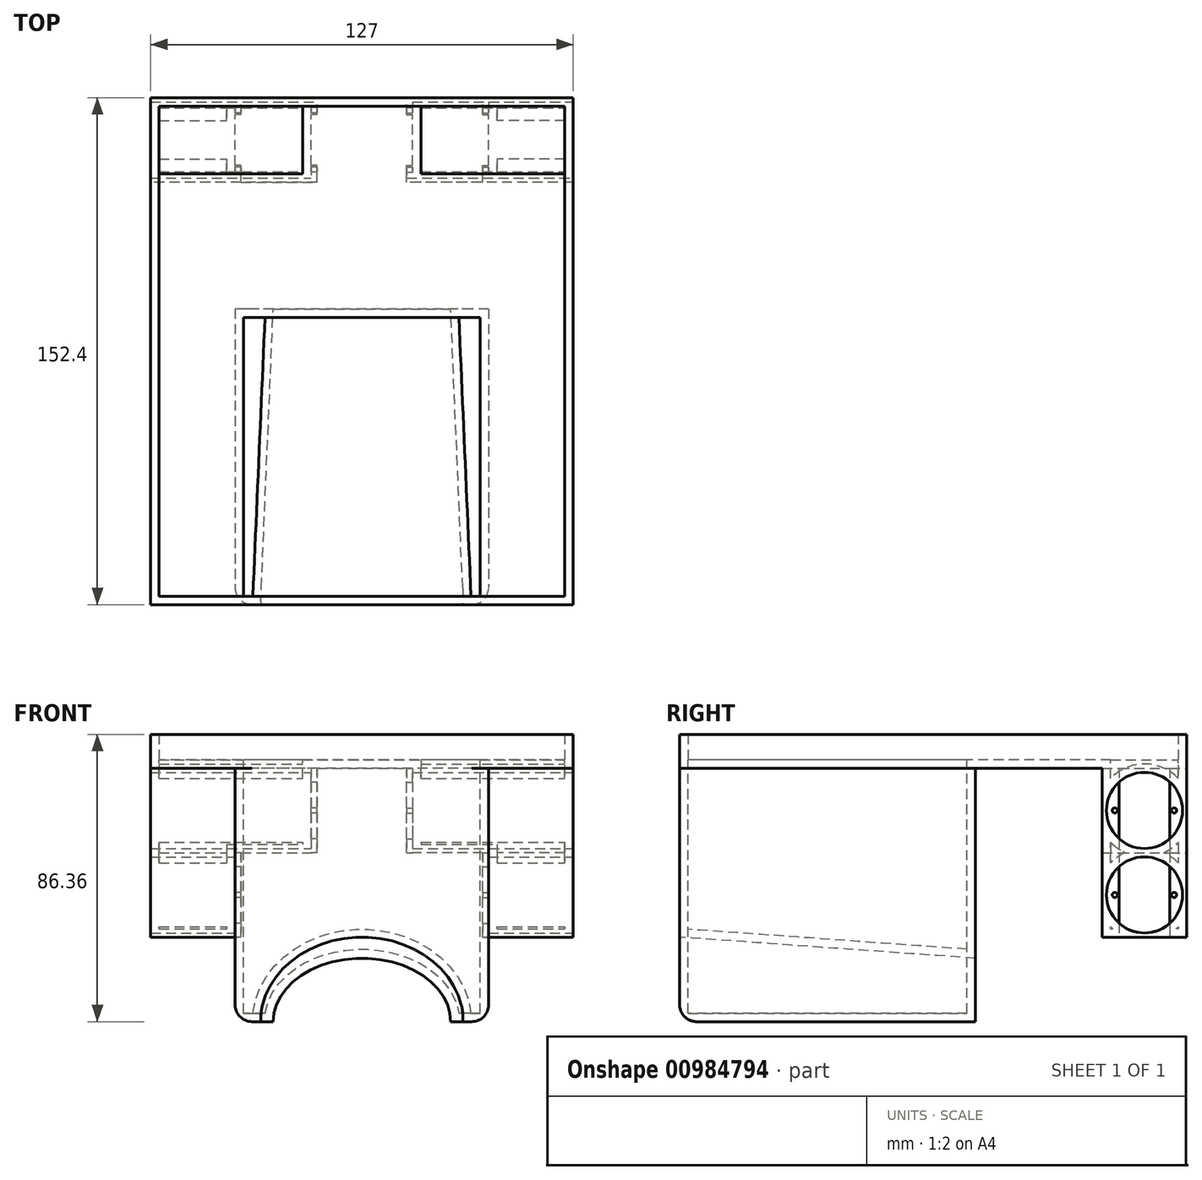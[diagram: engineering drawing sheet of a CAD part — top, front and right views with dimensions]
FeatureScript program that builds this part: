
annotation { "Feature Type Name" : "Feature", "Feature Type Description" : "" }
export const myFeature = defineFeature(function(context is Context, id is Id, definition is map)
    precondition{}
    {
        {
            var Q0;
            Q0=qCreatedBy(makeId("Top.planeOp"),FACE);
            var sketch = newSketch(context, id + "F0", { "sketchPlane" : qUnion([Q0])});
            skLineSegment(sketch, "E0.bottom", {"start": v(-89.57, 110.43) * mm, "end": v(12.03, 110.43) * mm});
            skLineSegment(sketch, "E0.top", {"start": v(-89.57, -41.97) * mm, "end": v(12.03, -41.97) * mm});
            skLineSegment(sketch, "E0.left", {"start": v(-89.57, 110.43) * mm, "end": v(-89.57, -41.97) * mm});
            skLineSegment(sketch, "E0.right", {"start": v(12.03, 110.43) * mm, "end": v(12.03, -41.97) * mm});
            skLineSegment(sketch, "E1", {"start": v(12.03, 110.43) * mm, "end": v(24.73, 110.43) * mm});
            skLineSegment(sketch, "E2", {"start": v(24.73, 110.43) * mm, "end": v(24.73, -41.97) * mm});
            skLineSegment(sketch, "E3", {"start": v(24.73, -41.97) * mm, "end": v(12.03, -41.97) * mm});
            skLineSegment(sketch, "E4.bottom", {"start": v(-89.57, 110.43) * mm, "end": v(-102.27, 110.43) * mm});
            skLineSegment(sketch, "E4.top", {"start": v(-89.57, -41.97) * mm, "end": v(-102.27, -41.97) * mm});
            skLineSegment(sketch, "E4.right", {"start": v(-102.27, 110.43) * mm, "end": v(-102.27, -41.97) * mm});
            skSolve(sketch);
        }
        {
            var Q0;
            Q0=makeQuery(id+"F0.imprint","IMPRINT",FACE,{"disambiguationData":[TD([[makeQuery(id+"F0.imprint","IMPRINT",EDGE,{"derivedFrom":sQuery(id+"F0.wireOp",EDGE,"E0.bottom")}),-1.0]])]});
            var Q1;
            Q1=makeQuery(id+"F0.imprint","IMPRINT",FACE,{"disambiguationData":[TD([[makeQuery(id+"F0.imprint","IMPRINT",EDGE,{"derivedFrom":sQuery(id+"F0.wireOp",EDGE,"E0.right")}),1.0]])]});
            var Q2;
            Q2=makeQuery(id+"F0.imprint","IMPRINT",FACE,{"disambiguationData":[TD([[makeQuery(id+"F0.imprint","IMPRINT",EDGE,{"derivedFrom":sQuery(id+"F0.wireOp",EDGE,"E4.bottom")}),1.0]])]});
            extrude(context, id + "F1", {"entities" : qUnion([Q0, Q1, Q2]), "depth" : 10.16 * mm, "offsetDistance" : 25.4 * mm});
        }
        {
            var Q0;
            Q0=makeQuery(id+"F1.opExtrude","CAP_FACE",FACE,{"disambiguationData":[OSD([sQuery(id+"F0.wireOp",EDGE,"E0.bottom"),sQuery(id+"F0.wireOp",EDGE,"E0.top"),sQuery(id+"F0.wireOp",EDGE,"E0.left"),sQuery(id+"F0.wireOp",EDGE,"E0.right")])],"isStart":true});
            var sketch = newSketch(context, id + "F2", { "sketchPlane" : qUnion([Q0])});
            skLineSegment(sketch, "E5", {"start": v(-38.77, -110.43) * mm, "end": v(-38.77, 53.26) * mm, "construction": true});
            skPoint(sketch, "E5.endSnap0", {"position": v(-38.77, 41.97) * mm});
            skLineSegment(sketch, "E6.bottom", {"start": v(-0.67, -46.93) * mm, "end": v(-76.87, -46.93) * mm});
            skLineSegment(sketch, "E6.top", {"start": v(-0.67, 41.97) * mm, "end": v(-76.87, 41.97) * mm});
            skLineSegment(sketch, "E6.left", {"start": v(-0.67, -46.93) * mm, "end": v(-0.67, 41.97) * mm});
            skLineSegment(sketch, "E6.right", {"start": v(-76.87, -46.93) * mm, "end": v(-76.87, 41.97) * mm});
            skLineSegment(sketch, "E7", {"start": v(-102.27, -34.23) * mm, "end": v(125.7, -34.23) * mm, "construction": true});
            skSolve(sketch);
        }
        {
            var Q0;
            Q0=makeQuery(id+"F2.imprint","IMPRINT",FACE,{"disambiguationData":[TD([[makeQuery(id+"F2.imprint","IMPRINT",EDGE,{"derivedFrom":sQuery(id+"F2.wireOp",EDGE,"E6.bottom")}),-1.0]])]});
            extrude(context, id + "F3", {"entities" : qUnion([Q0]), "operationType" : NewBodyOperationType.ADD, "depth" : 76.2 * mm, "offsetDistance" : 25.4 * mm});
        }
        {
            var Q0;
            Q0=makeQuery(id+"F3.boolean.opBoolean","MERGE",FACE,{"derivedFrom":[makeQuery(id+"F1.opExtrude","SWEPT_FACE",FACE,{"disambiguationData":[OSD([sQuery(id+"F0.wireOp",EDGE,"E0.top")])]}),makeQuery(id+"F3.opExtrude","SWEPT_FACE",FACE,{"disambiguationData":[OSD([sQuery(id+"F2.wireOp",EDGE,"E6.top")])]})]});
            var sketch = newSketch(context, id + "F4", { "sketchPlane" : qUnion([Q0])});
            skEllipse(sketch, "E8", {"center": v(-38.77, -76.2) * mm, "majorRadius": 30.48 * mm, "minorRadius": 25.4 * mm, "majorAxis": v(-1, 0)});
            skSolve(sketch);
        }
        {
            var Q0;
            Q0=makeQuery(id+"F3.opExtrude","SWEPT_FACE",FACE,{"disambiguationData":[OSD([sQuery(id+"F2.wireOp",EDGE,"E6.bottom")])]});
            var sketch = newSketch(context, id + "F5", { "sketchPlane" : qUnion([Q0])});
            skEllipse(sketch, "E9", {"center": v(38.77, -76.2) * mm, "majorRadius": 26.67 * mm, "minorRadius": 19.05 * mm, "majorAxis": v(-1, 0)});
            skSolve(sketch);
        }
        {
            var Q1;
            {var subQ0=sQuery(id+"F4.wireOp",EDGE,"E8");var subQ1=makeQuery(id+"F3.opExtrude","CAP_EDGE",EDGE,{"disambiguationData":[OSD([sQuery(id+"F2.wireOp",EDGE,"E6.top")])],"isStart":false});var subQ2=makeQuery(id+"F4.imprint","INTERSECT",VERTEX,{"disambiguationData":[OD(0.0)],"derivedFrom":[subQ1,subQ0]});Q1=makeQuery(id+"F4.imprint","IMPRINT",FACE,{"disambiguationData":[TD([[makeQuery(id+"F4.imprint","IMPRINT",EDGE,{"disambiguationData":[TD([[subQ2,1.0]])],"derivedFrom":subQ0}),1.0]])]});}
            var Q2;
            {var subQ0=sQuery(id+"F5.wireOp",EDGE,"E9");var subQ1=makeQuery(id+"F3.opExtrude","CAP_EDGE",EDGE,{"disambiguationData":[OSD([sQuery(id+"F2.wireOp",EDGE,"E6.bottom")])],"isStart":false});var subQ2=makeQuery(id+"F5.imprint","INTERSECT",VERTEX,{"disambiguationData":[OD(0.0)],"derivedFrom":[subQ1,subQ0]});Q2=makeQuery(id+"F5.imprint","IMPRINT",FACE,{"disambiguationData":[TD([[makeQuery(id+"F5.imprint","IMPRINT",EDGE,{"disambiguationData":[TD([[subQ2,1.0]])],"derivedFrom":subQ0}),1.0]])]});}
            loft(context, id + "F6", {"operationType" : NewBodyOperationType.REMOVE, "sheetProfilesArray" : [{ "sheetProfileEntities" : qUnion([Q1]) }, { "sheetProfileEntities" : qUnion([Q2]) }]});
        }
        {
            var Q0;
            Q0=makeQuery(id+"F0.imprint","IMPRINT",FACE,{"disambiguationData":[TD([[makeQuery(id+"F0.imprint","IMPRINT",EDGE,{"derivedFrom":sQuery(id+"F0.wireOp",EDGE,"E0.right")}),1.0]])]});
            extrude(context, id + "F7", {"entities" : qUnion([Q0]), "operationType" : NewBodyOperationType.ADD, "depth" : 10.16 * mm, "offsetDistance" : 25.4 * mm});
        }
        {
            var Q0;
            Q0=makeQuery(id+"F1.opExtrude","CAP_FACE",FACE,{"disambiguationData":[OSD([sQuery(id+"F0.wireOp",EDGE,"E0.bottom"),sQuery(id+"F0.wireOp",EDGE,"E0.top"),sQuery(id+"F0.wireOp",EDGE,"E1"),sQuery(id+"F0.wireOp",EDGE,"E2"),sQuery(id+"F0.wireOp",EDGE,"E3"),sQuery(id+"F0.wireOp",EDGE,"E4.bottom"),sQuery(id+"F0.wireOp",EDGE,"E4.top"),sQuery(id+"F0.wireOp",EDGE,"E4.right")])],"isStart":true});
            var sketch = newSketch(context, id + "F8", { "sketchPlane" : qUnion([Q0])});
            skLineSegment(sketch, "E10.bottom", {"start": v(24.73, -110.43) * mm, "end": v(-102.27, -110.43) * mm});
            skLineSegment(sketch, "E10.top", {"start": v(24.73, -85.03) * mm, "end": v(-102.27, -85.03) * mm});
            skLineSegment(sketch, "E10.left", {"start": v(24.73, -110.43) * mm, "end": v(24.73, -85.03) * mm});
            skLineSegment(sketch, "E10.right", {"start": v(-102.27, -110.43) * mm, "end": v(-102.27, -85.03) * mm});
            skSolve(sketch);
        }
        {
            var Q0;
            Q0=makeQuery(id+"F8.imprint","IMPRINT",FACE,{"disambiguationData":[TD([[makeQuery(id+"F8.imprint","IMPRINT",EDGE,{"derivedFrom":sQuery(id+"F8.wireOp",EDGE,"E10.bottom")}),1.0]])]});
            extrude(context, id + "F9", {"entities" : qUnion([Q0]), "operationType" : NewBodyOperationType.ADD, "depth" : 50.8 * mm, "offsetDistance" : 25.4 * mm});
        }
        {
            var Q0;
            Q0=makeQuery(id+"F9.boolean.opBoolean","MERGE",FACE,{"derivedFrom":[makeQuery(id+"F1.opExtrude","SWEPT_FACE",FACE,{"disambiguationData":[OSD([sQuery(id+"F0.wireOp",EDGE,"E0.bottom"),sQuery(id+"F0.wireOp",EDGE,"E1"),sQuery(id+"F0.wireOp",EDGE,"E4.bottom")])]}),makeQuery(id+"F9.opExtrude","SWEPT_FACE",FACE,{"disambiguationData":[OSD([sQuery(id+"F8.wireOp",EDGE,"E10.bottom")])]})]});
            var sketch = newSketch(context, id + "F10", { "sketchPlane" : qUnion([Q0])});
            skLineSegment(sketch, "E11", {"start": v(0.67, -50.8) * mm, "end": v(0.67, -25.4) * mm});
            skLineSegment(sketch, "E12", {"start": v(0.67, -25.4) * mm, "end": v(23.53, -25.4) * mm});
            skLineSegment(sketch, "E13", {"start": v(23.53, -25.4) * mm, "end": v(23.53, 0) * mm});
            skLineSegment(sketch, "E14", {"start": v(23.53, 0) * mm, "end": v(38.77, 0) * mm});
            skLineSegment(sketch, "E15", {"start": v(38.77, -50.8) * mm, "end": v(38.77, 29.87) * mm, "construction": true});
            skPoint(sketch, "E15.endSnap0", {"position": v(38.77, 10.16) * mm});
            skLineSegment(sketch, "E16.MirrorCS", {"start": v(54, -25.4) * mm, "end": v(54, 0) * mm});
            skLineSegment(sketch, "E17.MirrorCS", {"start": v(54, 0) * mm, "end": v(38.77, 0) * mm});
            skLineSegment(sketch, "E18.MirrorCS", {"start": v(76.87, -25.4) * mm, "end": v(54, -25.4) * mm});
            skLineSegment(sketch, "E19.MirrorCS", {"start": v(76.87, -50.8) * mm, "end": v(76.87, -25.4) * mm});
            skSolve(sketch);
        }
        {
            var Q0;
            {var subQ1=sQuery(id+"F10.wireOp",EDGE,"E11");Q0=makeQuery(id+"F10.imprint","IMPRINT",FACE,{"disambiguationData":[TD([[makeQuery(id+"F10.imprint","IMPRINT",EDGE,{"derivedFrom":subQ1}),-1.0]])]});}
            extrude(context, id + "F11", {"entities" : qUnion([Q0]), "operationType" : NewBodyOperationType.REMOVE, "oppositeDirection" : true, "depth" : 25.4 * mm, "offsetDistance" : 25.4 * mm});
        }
        {
            var Q0;
            Q0=makeQuery(id+"F9.boolean.opBoolean","MERGE",FACE,{"derivedFrom":[makeQuery(id+"F1.opExtrude","SWEPT_FACE",FACE,{"disambiguationData":[OSD([sQuery(id+"F0.wireOp",EDGE,"E2")])]}),makeQuery(id+"F9.opExtrude","SWEPT_FACE",FACE,{"disambiguationData":[OSD([sQuery(id+"F8.wireOp",EDGE,"E10.left")])]})]});
            var sketch = newSketch(context, id + "F12", { "sketchPlane" : qUnion([Q0])});
            skLineSegment(sketch, "E20", {"start": v(97.73, -50.8) * mm, "end": v(97.73, 17.2) * mm, "construction": true});
            skLineSegment(sketch, "E21", {"start": v(110.43, -38.1) * mm, "end": v(64.46, -38.1) * mm, "construction": true});
            skCircle(sketch, "E22", {"center": v(97.73, -38.1) * mm, "radius": 11.43 * mm});
            skCircle(sketch, "E23.0.1.0", {"center": v(97.73, -12.7) * mm, "radius": 11.43 * mm});
            skLineSegment(sketch, "E23.direction1", {"start": v(97.73, -38.1) * mm, "end": v(123.13, -38.1) * mm, "construction": true});
            skLineSegment(sketch, "E23.direction2", {"start": v(97.73, -38.1) * mm, "end": v(97.73, -12.7) * mm, "construction": true});
            skSolve(sketch);
        }
        {
            var Q0;
            Q0=makeQuery(id+"F12.imprint","IMPRINT",FACE,{"disambiguationData":[TD([[makeQuery(id+"F12.imprint","IMPRINT",EDGE,{"derivedFrom":sQuery(id+"F12.wireOp",EDGE,"E22")}),1.0]])]});
            var Q1;
            Q1=makeQuery(id+"F12.imprint","IMPRINT",FACE,{"disambiguationData":[TD([[makeQuery(id+"F12.imprint","IMPRINT",EDGE,{"derivedFrom":sQuery(id+"F12.wireOp",EDGE,"E23.0.1.0")}),1.0]])]});
            extrude(context, id + "F13", {"entities" : qUnion([Q0, Q1]), "operationType" : NewBodyOperationType.REMOVE, "endBound" : BoundingType.THROUGH_ALL, "oppositeDirection" : true, "depth" : 25.4 * mm, "offsetDistance" : 25.4 * mm});
        }
        {
            var Q0;
            Q0=makeQuery(id+"F11.boolean.opBoolean","COPY",FACE,{"derivedFrom":makeQuery(id+"F11.opExtrude","SWEPT_FACE",FACE,{"disambiguationData":[OSD([sQuery(id+"F10.wireOp",EDGE,"E11")])]})});
            var sketch = newSketch(context, id + "F14", { "sketchPlane" : qUnion([Q0])});
            skLineSegment(sketch, "E24.bottom", {"start": v(-110.43, -25.4) * mm, "end": v(-102.84, -25.4) * mm});
            skLineSegment(sketch, "E24.top", {"start": v(-110.43, -50.8) * mm, "end": v(-105.35, -50.8) * mm});
            skLineSegment(sketch, "E24.left", {"start": v(-110.43, -25.4) * mm, "end": v(-110.43, -50.8) * mm});
            skLineSegment(sketch, "E24.right", {"start": v(-105.35, -25.4) * mm, "end": v(-105.35, -50.8) * mm});
            skLineSegment(sketch, "E25", {"start": v(-97.73, -50.8) * mm, "end": v(-97.73, -40.1) * mm, "construction": true});
            skLineSegment(sketch, "E26", {"start": v(-110.43, -38.1) * mm, "end": v(-102.84, -38.1) * mm, "construction": true});
            skCircle(sketch, "E27", {"center": v(-106.63, -38.1) * mm, "radius": 0.77 * mm});
            skLineSegment(sketch, "E28.MirrorCS", {"start": v(-90.11, -25.4) * mm, "end": v(-90.11, -50.8) * mm});
            skLineSegment(sketch, "E29.MirrorCS", {"start": v(-85.03, -25.4) * mm, "end": v(-85.03, -50.8) * mm});
            skLineSegment(sketch, "E30.MirrorCS", {"start": v(-85.03, -50.8) * mm, "end": v(-90.11, -50.8) * mm});
            skLineSegment(sketch, "E31.MirrorCS", {"start": v(-85.03, -25.4) * mm, "end": v(-92.63, -25.4) * mm});
            skCircle(sketch, "E32.MirrorC", {"center": v(-88.83, -38.1) * mm, "radius": 0.77 * mm});
            skSolve(sketch);
        }
        {
            var Q0;
            Q0=makeQuery(id+"F14.imprint","IMPRINT",FACE,{"disambiguationData":[TD([[makeQuery(id+"F14.imprint","IMPRINT",EDGE,{"derivedFrom":sQuery(id+"F14.wireOp",EDGE,"E27")}),-1.0]])]});
            var Q1;
            Q1=makeQuery(id+"F14.imprint","IMPRINT",FACE,{"disambiguationData":[TD([[makeQuery(id+"F14.imprint","IMPRINT",EDGE,{"derivedFrom":sQuery(id+"F14.wireOp",EDGE,"E32.MirrorC")}),1.0]])]});
            var Q2;
            Q2=makeQuery(id+"F14.imprint","IMPRINT",FACE,{"disambiguationData":[TD([[makeQuery(id+"F14.imprint","IMPRINT",EDGE,{"derivedFrom":sQuery(id+"F14.wireOp",EDGE,"E29.MirrorCS")}),1.0]])]});
            var Q3;
            {var subQ7=sQuery(id+"F14.wireOp",EDGE,"E24.top");Q3=makeQuery(id+"F14.imprint","IMPRINT",FACE,{"disambiguationData":[TD([[makeQuery(id+"F14.imprint","IMPRINT",EDGE,{"derivedFrom":subQ7}),-1.0]])]});}
            extrude(context, id + "F15", {"entities" : qUnion([Q0, Q1, Q2, Q3]), "operationType" : NewBodyOperationType.ADD, "depth" : 1.78 * mm, "offsetDistance" : 25.4 * mm});
        }
        {
            var Q0;
            Q0=makeQuery(id+"F11.boolean.opBoolean","COPY",FACE,{"derivedFrom":makeQuery(id+"F11.opExtrude","SWEPT_FACE",FACE,{"disambiguationData":[OSD([sQuery(id+"F10.wireOp",EDGE,"E19.MirrorCS")])]})});
            var sketch = newSketch(context, id + "F16", { "sketchPlane" : qUnion([Q0])});
            skLineSegment(sketch, "E33.bottom", {"start": v(85.03, -25.4) * mm, "end": v(92.63, -25.4) * mm});
            skLineSegment(sketch, "E33.top", {"start": v(85.03, -50.8) * mm, "end": v(90.11, -50.8) * mm});
            skLineSegment(sketch, "E33.left", {"start": v(85.03, -25.4) * mm, "end": v(85.03, -50.8) * mm});
            skLineSegment(sketch, "E33.right", {"start": v(90.11, -25.4) * mm, "end": v(90.11, -50.8) * mm});
            skLineSegment(sketch, "E34", {"start": v(97.73, -50.8) * mm, "end": v(97.73, -40.1) * mm, "construction": true});
            skLineSegment(sketch, "E35", {"start": v(85.03, -38.1) * mm, "end": v(92.63, -38.1) * mm, "construction": true});
            skCircle(sketch, "E36", {"center": v(88.83, -38.1) * mm, "radius": 0.77 * mm});
            skLineSegment(sketch, "E37.MirrorCS", {"start": v(105.35, -25.4) * mm, "end": v(105.35, -50.8) * mm});
            skLineSegment(sketch, "E38.MirrorCS", {"start": v(110.43, -25.4) * mm, "end": v(110.43, -50.8) * mm});
            skLineSegment(sketch, "E39.MirrorCS", {"start": v(110.43, -50.8) * mm, "end": v(105.35, -50.8) * mm});
            skLineSegment(sketch, "E40.MirrorCS", {"start": v(110.43, -25.4) * mm, "end": v(102.84, -25.4) * mm});
            skCircle(sketch, "E41.MirrorC", {"center": v(106.63, -38.1) * mm, "radius": 0.77 * mm});
            skSolve(sketch);
        }
        {
            var Q0;
            Q0=makeQuery(id+"F16.imprint","IMPRINT",FACE,{"disambiguationData":[TD([[makeQuery(id+"F16.imprint","IMPRINT",EDGE,{"derivedFrom":sQuery(id+"F16.wireOp",EDGE,"E41.MirrorC")}),1.0]])]});
            var Q1;
            {var subQ1=sQuery(id+"F16.wireOp",EDGE,"E38.MirrorCS");Q1=makeQuery(id+"F16.imprint","IMPRINT",FACE,{"disambiguationData":[TD([[makeQuery(id+"F16.imprint","IMPRINT",EDGE,{"derivedFrom":subQ1}),1.0]])]});}
            var Q2;
            {var subQ7=sQuery(id+"F16.wireOp",EDGE,"E33.top");Q2=makeQuery(id+"F16.imprint","IMPRINT",FACE,{"disambiguationData":[TD([[makeQuery(id+"F16.imprint","IMPRINT",EDGE,{"derivedFrom":subQ7}),1.0]])]});}
            var Q3;
            Q3=makeQuery(id+"F16.imprint","IMPRINT",FACE,{"disambiguationData":[TD([[makeQuery(id+"F16.imprint","IMPRINT",EDGE,{"derivedFrom":sQuery(id+"F16.wireOp",EDGE,"E36")}),-1.0]])]});
            extrude(context, id + "F17", {"entities" : qUnion([Q0, Q1, Q2, Q3]), "operationType" : NewBodyOperationType.ADD, "depth" : 1.78 * mm, "offsetDistance" : 25.4 * mm});
        }
        {
            var Q0;
            Q0=makeQuery(id+"F11.boolean.opBoolean","COPY",FACE,{"derivedFrom":makeQuery(id+"F11.opExtrude","SWEPT_FACE",FACE,{"disambiguationData":[OSD([sQuery(id+"F10.wireOp",EDGE,"E16.MirrorCS")])]})});
            var sketch = newSketch(context, id + "F18", { "sketchPlane" : qUnion([Q0])});
            skLineSegment(sketch, "E42.bottom", {"start": v(85.03, 0) * mm, "end": v(92.63, 0) * mm});
            skLineSegment(sketch, "E42.top", {"start": v(85.03, -25.4) * mm, "end": v(90.11, -25.4) * mm});
            skLineSegment(sketch, "E42.left", {"start": v(85.03, 0) * mm, "end": v(85.03, -25.4) * mm});
            skLineSegment(sketch, "E42.right", {"start": v(90.11, 0) * mm, "end": v(90.11, -25.4) * mm});
            skLineSegment(sketch, "E43", {"start": v(97.73, -25.4) * mm, "end": v(97.73, -14.7) * mm, "construction": true});
            skLineSegment(sketch, "E44", {"start": v(85.03, -12.7) * mm, "end": v(92.63, -12.7) * mm, "construction": true});
            skCircle(sketch, "E45", {"center": v(88.83, -12.7) * mm, "radius": 0.77 * mm});
            skLineSegment(sketch, "E46.MirrorCS", {"start": v(105.35, 0) * mm, "end": v(105.35, -25.4) * mm});
            skLineSegment(sketch, "E47.MirrorCS", {"start": v(110.43, 0) * mm, "end": v(110.43, -25.4) * mm});
            skLineSegment(sketch, "E48.MirrorCS", {"start": v(110.43, -25.4) * mm, "end": v(105.35, -25.4) * mm});
            skLineSegment(sketch, "E49.MirrorCS", {"start": v(110.43, 0) * mm, "end": v(102.84, 0) * mm});
            skCircle(sketch, "E50.MirrorC", {"center": v(106.63, -12.7) * mm, "radius": 0.77 * mm});
            skSolve(sketch);
        }
        {
            var Q0;
            Q0=makeQuery(id+"F18.imprint","IMPRINT",FACE,{"disambiguationData":[TD([[makeQuery(id+"F18.imprint","IMPRINT",EDGE,{"derivedFrom":sQuery(id+"F18.wireOp",EDGE,"E45")}),-1.0]])]});
            var Q1;
            Q1=makeQuery(id+"F18.imprint","IMPRINT",FACE,{"disambiguationData":[TD([[makeQuery(id+"F18.imprint","IMPRINT",EDGE,{"derivedFrom":sQuery(id+"F18.wireOp",EDGE,"E50.MirrorC")}),1.0]])]});
            var Q2;
            {var subQ1=sQuery(id+"F18.wireOp",EDGE,"E47.MirrorCS");Q2=makeQuery(id+"F18.imprint","IMPRINT",FACE,{"disambiguationData":[TD([[makeQuery(id+"F18.imprint","IMPRINT",EDGE,{"derivedFrom":subQ1}),1.0]])]});}
            var Q3;
            {var subQ7=sQuery(id+"F18.wireOp",EDGE,"E42.top");Q3=makeQuery(id+"F18.imprint","IMPRINT",FACE,{"disambiguationData":[TD([[makeQuery(id+"F18.imprint","IMPRINT",EDGE,{"derivedFrom":subQ7}),1.0]])]});}
            extrude(context, id + "F19", {"entities" : qUnion([Q0, Q1, Q2, Q3]), "operationType" : NewBodyOperationType.ADD, "depth" : 1.78 * mm, "offsetDistance" : 25.4 * mm});
        }
        {
            var Q0;
            Q0=makeQuery(id+"F11.boolean.opBoolean","COPY",FACE,{"derivedFrom":makeQuery(id+"F11.opExtrude","SWEPT_FACE",FACE,{"disambiguationData":[OSD([sQuery(id+"F10.wireOp",EDGE,"E13")])]})});
            var sketch = newSketch(context, id + "F20", { "sketchPlane" : qUnion([Q0])});
            skLineSegment(sketch, "E51.bottom", {"start": v(-110.43, 0) * mm, "end": v(-102.84, 0) * mm});
            skLineSegment(sketch, "E51.top", {"start": v(-110.43, -25.4) * mm, "end": v(-105.35, -25.4) * mm});
            skLineSegment(sketch, "E51.left", {"start": v(-110.43, 0) * mm, "end": v(-110.43, -25.4) * mm});
            skLineSegment(sketch, "E51.right", {"start": v(-105.35, 0) * mm, "end": v(-105.35, -25.4) * mm});
            skLineSegment(sketch, "E52", {"start": v(-97.73, -25.4) * mm, "end": v(-97.73, -14.7) * mm, "construction": true});
            skLineSegment(sketch, "E53", {"start": v(-110.43, -12.7) * mm, "end": v(-102.84, -12.7) * mm, "construction": true});
            skCircle(sketch, "E54", {"center": v(-106.63, -12.7) * mm, "radius": 0.77 * mm});
            skLineSegment(sketch, "E55.MirrorCS", {"start": v(-90.11, 0) * mm, "end": v(-90.11, -25.4) * mm});
            skLineSegment(sketch, "E56.MirrorCS", {"start": v(-85.03, 0) * mm, "end": v(-85.03, -25.4) * mm});
            skLineSegment(sketch, "E57.MirrorCS", {"start": v(-85.03, -25.4) * mm, "end": v(-90.11, -25.4) * mm});
            skLineSegment(sketch, "E58.MirrorCS", {"start": v(-85.03, 0) * mm, "end": v(-92.63, 0) * mm});
            skCircle(sketch, "E59.MirrorC", {"center": v(-88.83, -12.7) * mm, "radius": 0.77 * mm});
            skSolve(sketch);
        }
        {
            var Q0;
            {var subQ1=sQuery(id+"F20.wireOp",EDGE,"E56.MirrorCS");Q0=makeQuery(id+"F20.imprint","IMPRINT",FACE,{"disambiguationData":[TD([[makeQuery(id+"F20.imprint","IMPRINT",EDGE,{"derivedFrom":subQ1}),1.0]])]});}
            var Q1;
            Q1=makeQuery(id+"F20.imprint","IMPRINT",FACE,{"disambiguationData":[TD([[makeQuery(id+"F20.imprint","IMPRINT",EDGE,{"derivedFrom":sQuery(id+"F20.wireOp",EDGE,"E59.MirrorC")}),1.0]])]});
            var Q2;
            Q2=makeQuery(id+"F20.imprint","IMPRINT",FACE,{"disambiguationData":[TD([[makeQuery(id+"F20.imprint","IMPRINT",EDGE,{"derivedFrom":sQuery(id+"F20.wireOp",EDGE,"E54")}),-1.0]])]});
            var Q3;
            {var subQ7=sQuery(id+"F20.wireOp",EDGE,"E51.top");Q3=makeQuery(id+"F20.imprint","IMPRINT",FACE,{"disambiguationData":[TD([[makeQuery(id+"F20.imprint","IMPRINT",EDGE,{"derivedFrom":subQ7}),-1.0]])]});}
            extrude(context, id + "F21", {"entities" : qUnion([Q0, Q1, Q2, Q3]), "operationType" : NewBodyOperationType.ADD, "depth" : 1.78 * mm, "offsetDistance" : 25.4 * mm});
        }
        {
            var Q0;
            Q0=makeQuery(id+"F1.opExtrude","CAP_FACE",FACE,{"disambiguationData":[OSD([sQuery(id+"F0.wireOp",EDGE,"E0.bottom"),sQuery(id+"F0.wireOp",EDGE,"E0.top"),sQuery(id+"F0.wireOp",EDGE,"E1"),sQuery(id+"F0.wireOp",EDGE,"E2"),sQuery(id+"F0.wireOp",EDGE,"E3"),sQuery(id+"F0.wireOp",EDGE,"E4.bottom"),sQuery(id+"F0.wireOp",EDGE,"E4.top"),sQuery(id+"F0.wireOp",EDGE,"E4.right")])],"isStart":false});
            shell(context, id + "F22", {"entities" : qUnion([Q0]), "thickness" : 2.54 * mm});
        }
        {
            var Q0;
            Q0=makeQuery(id+"F3.opExtrude","CAP_EDGE",EDGE,{"disambiguationData":[OSD([sQuery(id+"F2.wireOp",EDGE,"E6.right")])],"isStart":false});
            var Q1;
            {var subQ0=sQuery(id+"F5.wireOp",EDGE,"E9");var subQ1=sQuery(id+"F2.wireOp",EDGE,"E6.bottom");var subQ2=sQuery(id+"F4.wireOp",EDGE,"E8");var subQ3=sQuery(id+"F2.wireOp",EDGE,"E6.top");Q1=makeQuery(id+"F6.boolean.opBoolean","COPY",EDGE,{"derivedFrom":makeQuery(id+"F6.opLoft","SWEPT_EDGE",EDGE,{"disambiguationData":[OSD([subQ1,subQ3,subQ2,subQ0]),TDD([makeQuery(id+"F4.imprint","INTERSECT",VERTEX,{"disambiguationData":[OD(0.0)],"derivedFrom":[makeQuery(id+"F3.opExtrude","CAP_EDGE",EDGE,{"disambiguationData":[OSD([subQ3])],"isStart":false}),subQ2]}),makeQuery(id+"F5.imprint","INTERSECT",VERTEX,{"disambiguationData":[OD(1.0)],"derivedFrom":[makeQuery(id+"F3.opExtrude","CAP_EDGE",EDGE,{"disambiguationData":[OSD([subQ1])],"isStart":false}),subQ0]})])]})});}
            var Q2;
            {var subQ0=sQuery(id+"F5.wireOp",EDGE,"E9");var subQ1=sQuery(id+"F2.wireOp",EDGE,"E6.bottom");var subQ2=sQuery(id+"F4.wireOp",EDGE,"E8");var subQ3=sQuery(id+"F2.wireOp",EDGE,"E6.top");Q2=makeQuery(id+"F6.boolean.opBoolean","COPY",EDGE,{"derivedFrom":makeQuery(id+"F6.opLoft","SWEPT_EDGE",EDGE,{"disambiguationData":[OSD([subQ1,subQ3,subQ2,subQ0]),TDD([makeQuery(id+"F4.imprint","INTERSECT",VERTEX,{"disambiguationData":[OD(1.0)],"derivedFrom":[makeQuery(id+"F3.opExtrude","CAP_EDGE",EDGE,{"disambiguationData":[OSD([subQ3])],"isStart":false}),subQ2]}),makeQuery(id+"F5.imprint","INTERSECT",VERTEX,{"disambiguationData":[OD(0.0)],"derivedFrom":[makeQuery(id+"F3.opExtrude","CAP_EDGE",EDGE,{"disambiguationData":[OSD([subQ1])],"isStart":false}),subQ0]})])]})});}
            var Q3;
            Q3=makeQuery(id+"F3.opExtrude","CAP_EDGE",EDGE,{"disambiguationData":[OSD([sQuery(id+"F2.wireOp",EDGE,"E6.left")])],"isStart":false});
            fillet(context, id + "F23", {"entities" : qUnion([Q0, Q1, Q2, Q3]), "radius" : 5.08 * mm, "tangentPropagation" : true, "allowEdgeOverflow" : false});
        }
        {
            var Q0;
            Q0=makeQuery(id+"F3.opExtrude","SWEPT_EDGE",EDGE,{"disambiguationData":[OSD([sQuery(id+"F0.wireOp",EDGE,"E0.top"),sQuery(id+"F0.wireOp",EDGE,"E3"),sQuery(id+"F0.wireOp",EDGE,"E4.top"),sQuery(id+"F2.wireOp",EDGE,"E6.top"),sQuery(id+"F2.wireOp",EDGE,"E6.right")])]});
            var Q1;
            Q1=makeQuery(id+"F3.opExtrude","SWEPT_EDGE",EDGE,{"disambiguationData":[OSD([sQuery(id+"F0.wireOp",EDGE,"E0.top"),sQuery(id+"F0.wireOp",EDGE,"E3"),sQuery(id+"F0.wireOp",EDGE,"E4.top"),sQuery(id+"F2.wireOp",EDGE,"E6.top"),sQuery(id+"F2.wireOp",EDGE,"E6.left")])]});
            var Q2;
            {var subQ0=sQuery(id+"F5.wireOp",EDGE,"E9");var subQ1=sQuery(id+"F2.wireOp",EDGE,"E6.bottom");var subQ2=makeQuery(id+"F3.opExtrude","CAP_EDGE",EDGE,{"disambiguationData":[OSD([subQ1])],"isStart":false});var subQ3=makeQuery(id+"F5.imprint","INTERSECT",VERTEX,{"disambiguationData":[OD(0.0)],"derivedFrom":[subQ2,subQ0]});var subQ4=makeQuery(id+"F5.imprint","INTERSECT",VERTEX,{"disambiguationData":[OD(1.0)],"derivedFrom":[subQ2,subQ0]});Q2=makeQuery(id+"F6.boolean.opBoolean","COPY",EDGE,{"derivedFrom":makeQuery(id+"F6.opLoft","MID_CAP_EDGE",EDGE,{"disambiguationData":[OSD([subQ1,subQ0]),TDD([subQ3,subQ4,makeQuery(id+"F5.imprint","IMPRINT",EDGE,{"disambiguationData":[TD([[subQ3,1.0]])],"derivedFrom":subQ0})])],"capPos":1.0})});}
            fillet(context, id + "F24", {"entities" : qUnion([Q0, Q1, Q2]), "radius" : 5.08 * mm, "tangentPropagation" : true, "allowEdgeOverflow" : false});
        }
    });
